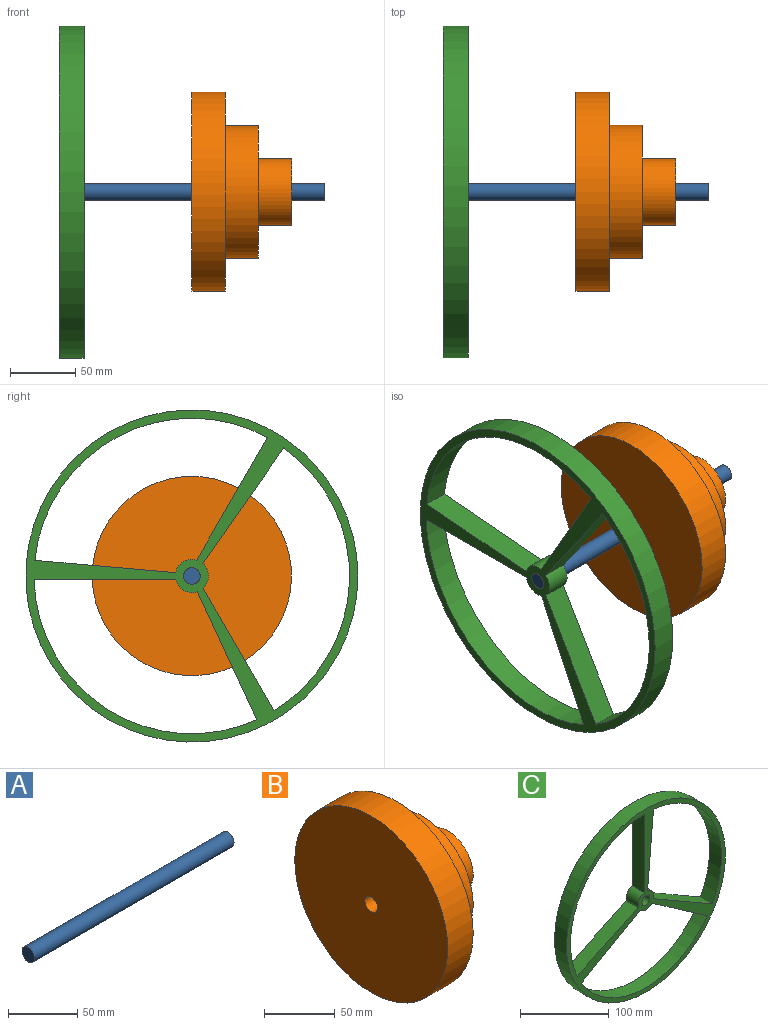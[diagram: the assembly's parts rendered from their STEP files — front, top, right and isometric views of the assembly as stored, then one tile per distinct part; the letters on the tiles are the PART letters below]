
ASSEMBLY  parts=3 mates=2
PART A: 3 faces, bbox 203.2x12.7x12.7 mm
  f0: cylinder r=6.35mm len=203.2mm, axis (-1,0,0), area 8107.3mm2, adj f1,f2
  f1: plane 12.7x12.7mm, normal (1,0,0), area 126.7mm2, adj f0
  f2: plane 12.7x12.7mm, normal (-1,0,0), area 126.7mm2, adj f0
PART B: 8 faces, bbox 76.2x152.4x152.4 mm
  f0: cylinder r=76.2mm len=152.4mm, axis (-1,0,0), area 12161mm2, adj f1,f2
  f1: plane 152.4x152.4mm, normal (1,0,0), area 10134.1mm2, adj f0,f3
  f2: plane 152.4x152.4mm, normal (-1,0,0), area 18114.8mm2, adj f0,f7
  f3: cylinder r=50.8mm len=101.6mm, axis (-1,0,0), area 8107.3mm2, adj f1,f4
  f4: plane 101.6x101.6mm, normal (1,0,0), area 6080.5mm2, adj f3,f5
  f5: cylinder r=25.4mm len=50.8mm, axis (-1,0,0), area 4053.7mm2, adj f4,f6
  f6: plane 50.8x50.8mm, normal (1,0,0), area 1900.2mm2, adj f5,f7
  f7: cylinder r=6.35mm len=76.2mm, axis (1,0,0), area 3040.2mm2, adj f2,f6
PART C: 16 faces, bbox 254x19.1x254 mm
  f0: plane 97.9x45.65mm, normal (-0.42,0,0.91), area 2057.9mm2, adj f1,f10,f14,f15
  f1: cylinder r=120.65mm len=170.27mm, axis (0,1,0), area 4530mm2, adj f0,f2,f14,f15
  f2: plane 108.25x19.05mm, normal (-1,0,0), area 2062.2mm2, adj f1,f10,f14,f15
  f3: cylinder r=120.65mm len=200.99mm, axis (0,1,0), area 4530mm2, adj f4,f11,f14,f15
  f4: plane 93.75x54.13mm, normal (0.5,0,-0.87), area 2062.2mm2, adj f3,f5,f14,f15
  f5: cylinder r=12.7mm len=19.05mm, axis (0,1,0), area 401.9mm2, adj f4,f11,f14,f15
  f6: cylinder r=120.65mm len=177.85mm, axis (0,1,0), area 4530mm2, adj f7,f12,f14,f15
  f7: plane 93.75x54.13mm, normal (0.5,0,0.87), area 2062.2mm2, adj f6,f8,f14,f15
  f8: cylinder r=12.7mm len=19.05mm, axis (0,1,0), area 401.9mm2, adj f7,f12,f14,f15
  f9: cylinder r=127mm len=254mm, axis (0,1,0), area 15201.2mm2, adj f14,f15
  f10: cylinder r=12.7mm len=19.05mm, axis (0,1,0), area 401.9mm2, adj f0,f2,f14,f15
  f11: plane 88.49x61.96mm, normal (-0.57,0,-0.82), area 2057.9mm2, adj f3,f5,f14,f15
  f12: plane 107.61x19.05mm, normal (1,0,-0.09), area 2057.9mm2, adj f6,f8,f14,f15
  f13: cylinder r=6.35mm len=19.05mm, axis (0,1,0), area 760.1mm2, adj f14,f15
  f14: plane 254x254mm, normal (0,-1,0), area 8619.3mm2, adj f0,f1,f2,f3,f4,f5,f6,f7
  f15: plane 254x254mm, normal (0,1,0), area 8619.3mm2, adj f0,f1,f2,f3,f4,f5,f6,f7
PLACE A rot(axis=(0,1,0),180deg) t=(203.2,0,0)mm
PLACE B rot(axis=(1,0,0),180deg) t=(101.6,0,0)mm
PLACE C rot(axis=(-0.58,-0.58,-0.58),120deg) t=(19.05,0,0)mm
MATE fastened B.f7 <-> A.f0  axis (-1,0,0) through (101.6,0,0)mm
MATE fastened C.f10 <-> A.f0  axis (-1,0,0) through (0,0,0)mm
